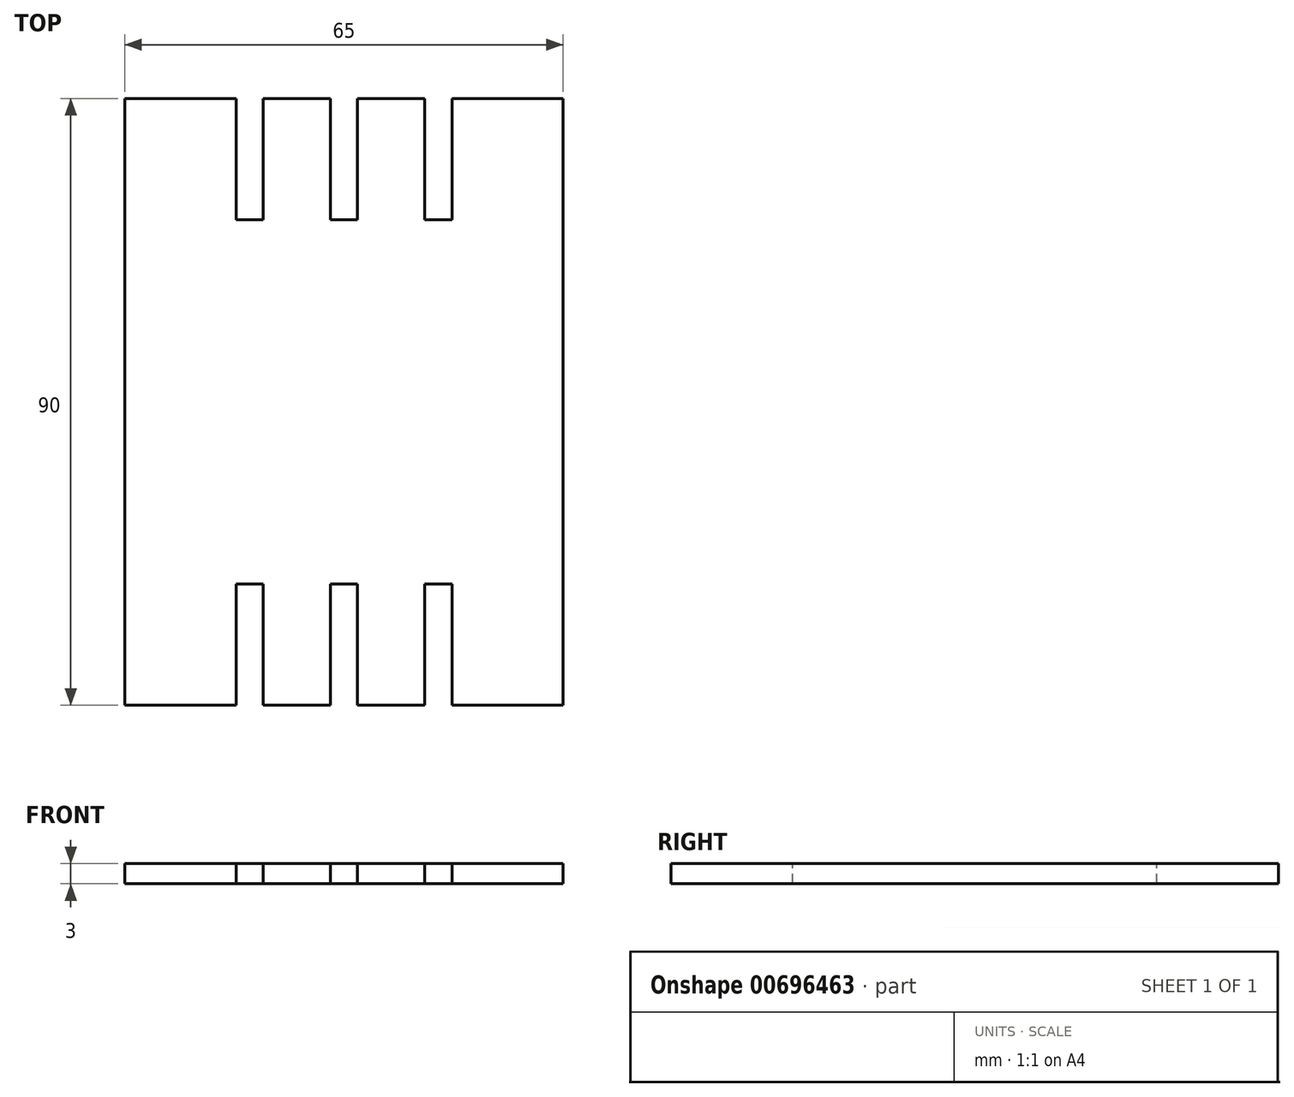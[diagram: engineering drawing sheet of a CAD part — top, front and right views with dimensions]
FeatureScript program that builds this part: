
annotation { "Feature Type Name" : "Feature", "Feature Type Description" : "" }
export const myFeature = defineFeature(function(context is Context, id is Id, definition is map)
    precondition{}
    {
        {
            var Q0;
            Q0=qCreatedBy(makeId("Top.planeOp"),FACE);
            var sketch = newSketch(context, id + "F0", { "sketchPlane" : qUnion([Q0])});
            skLineSegment(sketch, "E0.bottom", {"start": v(32.5, 45) * mm, "end": v(-32.5, 45) * mm});
            skLineSegment(sketch, "E0.top", {"start": v(32.5, -45) * mm, "end": v(-32.5, -45) * mm});
            skLineSegment(sketch, "E0.left", {"start": v(32.5, 45) * mm, "end": v(32.5, -45) * mm});
            skLineSegment(sketch, "E0.right", {"start": v(-32.5, 45) * mm, "end": v(-32.5, -45) * mm});
            skPoint(sketch, "E0.middle", {"position": v(0, 0) * mm});
            skSolve(sketch);
        }
        {
            var Q0;
            Q0=makeQuery(id+"F0.imprint","IMPRINT",FACE,{"disambiguationData":[TD([[makeQuery(id+"F0.imprint","IMPRINT",EDGE,{"derivedFrom":sQuery(id+"F0.wireOp",EDGE,"E0.bottom")}),1.0]])]});
            extrude(context, id + "F1", {"entities" : qUnion([Q0]), "depth" : 3 * mm, "offsetDistance" : 25.4 * mm});
        }
        {
            var Q0;
            Q0=makeQuery(id+"F1.opExtrude","CAP_FACE",FACE,{"disambiguationData":[OSD([sQuery(id+"F0.wireOp",EDGE,"E0.bottom"),sQuery(id+"F0.wireOp",EDGE,"E0.top"),sQuery(id+"F0.wireOp",EDGE,"E0.left"),sQuery(id+"F0.wireOp",EDGE,"E0.right")])],"isStart":false});
            var sketch = newSketch(context, id + "F2", { "sketchPlane" : qUnion([Q0])});
            skLineSegment(sketch, "E1.bottom", {"start": v(-16, -45) * mm, "end": v(-12, -45) * mm});
            skLineSegment(sketch, "E1.top", {"start": v(-16, -27) * mm, "end": v(-12, -27) * mm});
            skLineSegment(sketch, "E1.left", {"start": v(-16, -45) * mm, "end": v(-16, -27) * mm});
            skLineSegment(sketch, "E1.right", {"start": v(-12, -45) * mm, "end": v(-12, -27) * mm});
            skLineSegment(sketch, "E2.bottom", {"start": v(-2, -45) * mm, "end": v(2, -45) * mm});
            skLineSegment(sketch, "E2.top", {"start": v(-2, -27) * mm, "end": v(2, -27) * mm});
            skLineSegment(sketch, "E2.left", {"start": v(-2, -45) * mm, "end": v(-2, -27) * mm});
            skLineSegment(sketch, "E2.right", {"start": v(2, -45) * mm, "end": v(2, -27) * mm});
            skLineSegment(sketch, "E3.bottom", {"start": v(12, -45) * mm, "end": v(16, -45) * mm});
            skLineSegment(sketch, "E3.top", {"start": v(12, -27) * mm, "end": v(16, -27) * mm});
            skLineSegment(sketch, "E3.left", {"start": v(12, -45) * mm, "end": v(12, -27) * mm});
            skLineSegment(sketch, "E3.right", {"start": v(16, -45) * mm, "end": v(16, -27) * mm});
            skLineSegment(sketch, "E4.MirrorCS", {"start": v(2, 45) * mm, "end": v(2, 27) * mm});
            skLineSegment(sketch, "E5.MirrorCS", {"start": v(-2, 45) * mm, "end": v(2, 45) * mm});
            skLineSegment(sketch, "E6.MirrorCS", {"start": v(12, 27) * mm, "end": v(16, 27) * mm});
            skLineSegment(sketch, "E7.MirrorCS", {"start": v(12, 45) * mm, "end": v(16, 45) * mm});
            skLineSegment(sketch, "E8.MirrorCS", {"start": v(-2, 27) * mm, "end": v(2, 27) * mm});
            skLineSegment(sketch, "E9.MirrorCS", {"start": v(-16, 27) * mm, "end": v(-12, 27) * mm});
            skLineSegment(sketch, "E10.MirrorCS", {"start": v(16, 45) * mm, "end": v(16, 27) * mm});
            skLineSegment(sketch, "E11.MirrorCS", {"start": v(12, 45) * mm, "end": v(12, 27) * mm});
            skLineSegment(sketch, "E12.MirrorCS", {"start": v(-2, 45) * mm, "end": v(-2, 27) * mm});
            skLineSegment(sketch, "E13.MirrorCS", {"start": v(-12, 45) * mm, "end": v(-12, 27) * mm});
            skLineSegment(sketch, "E14.MirrorCS", {"start": v(-16, 45) * mm, "end": v(-12, 45) * mm});
            skLineSegment(sketch, "E15.MirrorCS", {"start": v(-16, 45) * mm, "end": v(-16, 27) * mm});
            skSolve(sketch);
        }
        {
            var Q0;
            Q0 = qSketchRegion(id + "F2", true);
            extrude(context, id + "F3", {"entities" : qUnion([Q0]), "operationType" : NewBodyOperationType.REMOVE, "endBound" : BoundingType.THROUGH_ALL, "oppositeDirection" : true, "depth" : 25 * mm, "offsetDistance" : 25 * mm});
        }
    });
